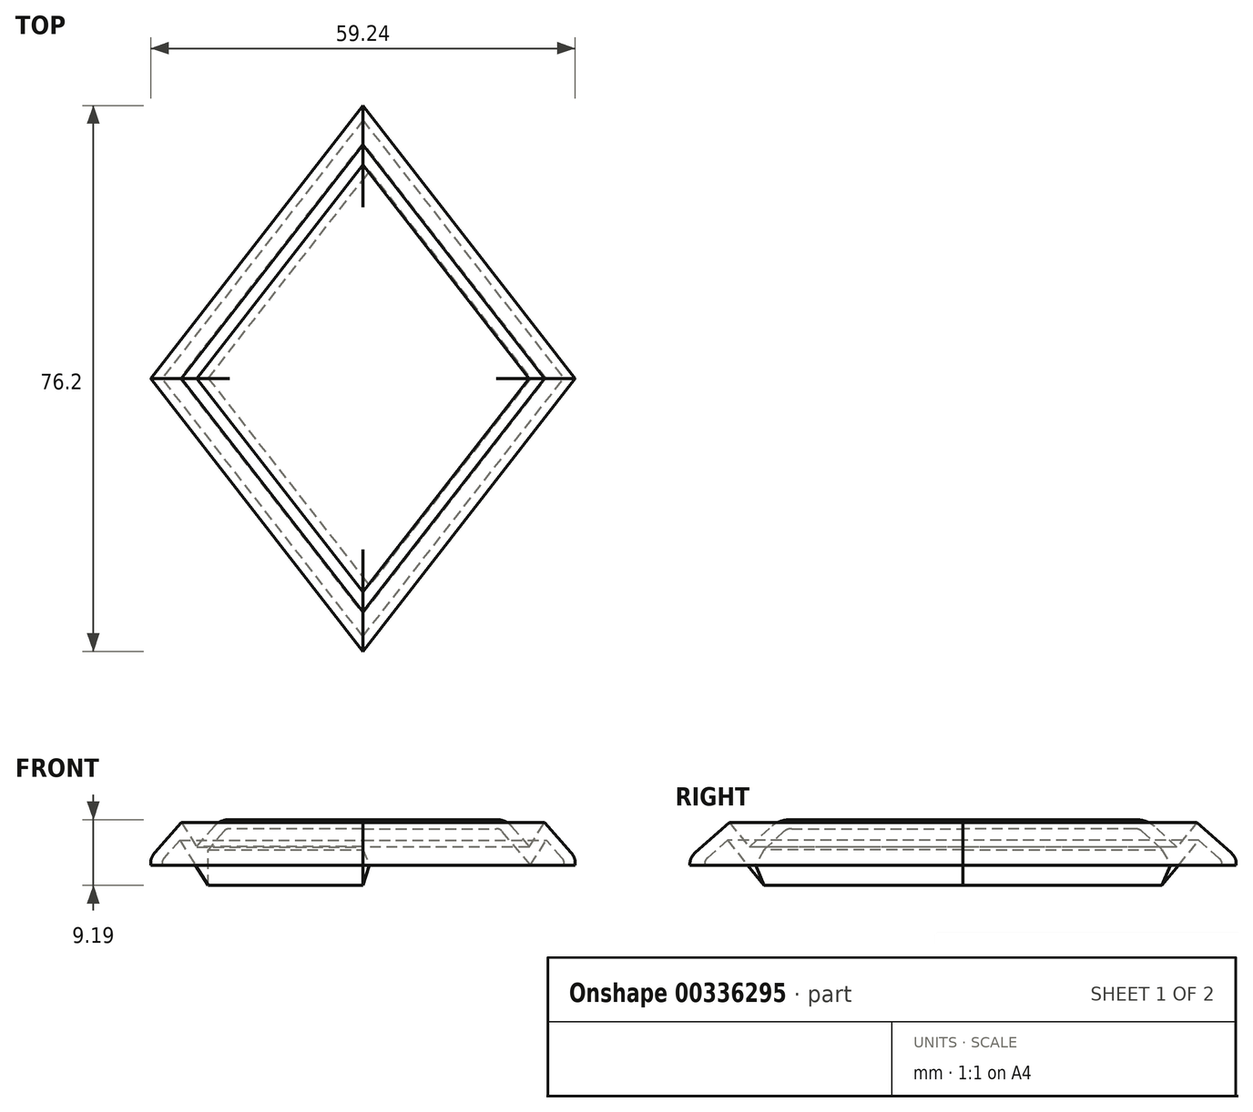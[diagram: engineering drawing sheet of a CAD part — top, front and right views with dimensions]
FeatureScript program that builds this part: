
annotation { "Feature Type Name" : "Feature", "Feature Type Description" : "" }
export const myFeature = defineFeature(function(context is Context, id is Id, definition is map)
    precondition{}
    {
        {
            var Q0;
            Q0=qCreatedBy(makeId("Top.planeOp"),FACE);
            var sketch = newSketch(context, id + "F0", { "sketchPlane" : qUnion([Q0])});
            skLineSegment(sketch, "E0", {"start": v(0, 38.1) * mm, "end": v(-29.62, 0) * mm});
            skLineSegment(sketch, "E1.MirrorCS", {"start": v(0, 38.1) * mm, "end": v(29.62, 0) * mm});
            skLineSegment(sketch, "E2.MirrorCS", {"start": v(0, -38.1) * mm, "end": v(-29.62, 0) * mm});
            skLineSegment(sketch, "E3.MirrorCS", {"start": v(0, -38.1) * mm, "end": v(29.62, 0) * mm});
            skLineSegment(sketch, "E4.0", {"start": v(0, -29.82) * mm, "end": v(23.18, 0) * mm});
            skLineSegment(sketch, "E4.1", {"start": v(0, -29.82) * mm, "end": v(-23.18, 0) * mm});
            skLineSegment(sketch, "E4.2", {"start": v(0, 29.82) * mm, "end": v(-23.18, 0) * mm});
            skLineSegment(sketch, "E4.3", {"start": v(0, 29.82) * mm, "end": v(23.18, 0) * mm});
            skSolve(sketch);
        }
        {
            var Q0;
            Q0=makeQuery(id+"F0.imprint","IMPRINT",FACE,{"disambiguationData":[TD([[makeQuery(id+"F0.imprint","IMPRINT",EDGE,{"derivedFrom":sQuery(id+"F0.wireOp",EDGE,"E0")}),1.0]])]});
            extrude(context, id + "F1", {"entities" : qUnion([Q0]), "depth" : 7.62 * mm});
        }
        {
            var Q0;
            Q0=makeQuery(id+"F1.opExtrude","CAP_EDGE",EDGE,{"disambiguationData":[OSD([sQuery(id+"F0.wireOp",EDGE,"E0")])],"isStart":false});
            var Q1;
            Q1=makeQuery(id+"F1.opExtrude","CAP_EDGE",EDGE,{"disambiguationData":[OSD([sQuery(id+"F0.wireOp",EDGE,"E2.MirrorCS")])],"isStart":false});
            var Q2;
            Q2=makeQuery(id+"F1.opExtrude","CAP_EDGE",EDGE,{"disambiguationData":[OSD([sQuery(id+"F0.wireOp",EDGE,"E3.MirrorCS")])],"isStart":false});
            var Q3;
            Q3=makeQuery(id+"F1.opExtrude","CAP_EDGE",EDGE,{"disambiguationData":[OSD([sQuery(id+"F0.wireOp",EDGE,"E1.MirrorCS")])],"isStart":false});
            chamfer(context, id + "F2", {"entities" : qUnion([Q0, Q1, Q2, Q3]), "chamferType" : ChamferType.OFFSET_ANGLE, "width" : 4.57 * mm, "oppositeDirection" : false, "angle" : 55 * degree, "tangentPropagation" : true});
        }
        {
            var Q0;
            Q0=makeQuery(id+"F1.opExtrude","CAP_EDGE",EDGE,{"disambiguationData":[OSD([sQuery(id+"F0.wireOp",EDGE,"E4.3")])],"isStart":false});
            var Q1;
            Q1=makeQuery(id+"F1.opExtrude","CAP_EDGE",EDGE,{"disambiguationData":[OSD([sQuery(id+"F0.wireOp",EDGE,"E4.2")])],"isStart":false});
            var Q2;
            Q2=makeQuery(id+"F1.opExtrude","CAP_EDGE",EDGE,{"disambiguationData":[OSD([sQuery(id+"F0.wireOp",EDGE,"E4.1")])],"isStart":false});
            var Q3;
            Q3=makeQuery(id+"F1.opExtrude","CAP_EDGE",EDGE,{"disambiguationData":[OSD([sQuery(id+"F0.wireOp",EDGE,"E4.0")])],"isStart":false});
            chamfer(context, id + "F3", {"entities" : qUnion([Q0, Q1, Q2, Q3]), "chamferType" : ChamferType.TWO_OFFSETS, "width1" : 2.54 * mm, "oppositeDirection" : false, "width2" : 5.08 * mm, "tangentPropagation" : true});
        }
        {
            var Q0;
            Q0=makeQuery(id+"F0.imprint","IMPRINT",FACE,{"disambiguationData":[TD([[makeQuery(id+"F0.imprint","IMPRINT",EDGE,{"derivedFrom":sQuery(id+"F0.wireOp",EDGE,"E4.2")}),1.0]])]});
            extrude(context, id + "F4", {"entities" : qUnion([Q0]), "depth" : 6.35 * mm});
        }
        {
            var Q0;
            Q0=makeQuery(id+"F4.opExtrude","CAP_FACE",FACE,{"disambiguationData":[OSD([sQuery(id+"F0.wireOp",EDGE,"E4.2"),sQuery(id+"F0.wireOp",EDGE,"E4.3"),sQuery(id+"F0.wireOp",EDGE,"E4.0"),sQuery(id+"F0.wireOp",EDGE,"E4.1")])],"isStart":false});
            chamfer(context, id + "F5", {"entities" : qUnion([Q0]), "chamferType" : ChamferType.TWO_OFFSETS, "width1" : 2.54 * mm, "oppositeDirection" : false, "width2" : 3.8 * mm, "tangentPropagation" : true});
        }
        {
            var Q0;
            Q0=makeQuery(id+"F4.opExtrude","CAP_FACE",FACE,{"disambiguationData":[OSD([sQuery(id+"F0.wireOp",EDGE,"E4.2"),sQuery(id+"F0.wireOp",EDGE,"E4.3"),sQuery(id+"F0.wireOp",EDGE,"E4.0"),sQuery(id+"F0.wireOp",EDGE,"E4.1")])],"isStart":false});
            fillet(context, id + "F6", {"entities" : qUnion([Q0]), "radius" : 2.03 * mm, "tangentPropagation" : true, "allowEdgeOverflow" : false});
        }
        {
            var Q0;
            {var subQ0=sQuery(id+"F0.wireOp",EDGE,"E2.MirrorCS");Q0=makeQuery(id+"F2.opChamfer","BLEND_EDGE",EDGE,{"blendedFrom":[makeQuery(id+"F1.opExtrude","CAP_EDGE",EDGE,{"disambiguationData":[OSD([subQ0])],"isStart":false}),makeQuery(id+"F1.opExtrude","SWEPT_FACE",FACE,{"disambiguationData":[OSD([subQ0])]})],"blendedInto":[makeQuery(id+"F1.opExtrude","SWEPT_FACE",FACE,{"disambiguationData":[OSD([subQ0])]})]});}
            var Q1;
            {var subQ0=sQuery(id+"F0.wireOp",EDGE,"E0");Q1=makeQuery(id+"F2.opChamfer","BLEND_EDGE",EDGE,{"blendedFrom":[makeQuery(id+"F1.opExtrude","CAP_EDGE",EDGE,{"disambiguationData":[OSD([subQ0])],"isStart":false}),makeQuery(id+"F1.opExtrude","SWEPT_FACE",FACE,{"disambiguationData":[OSD([subQ0])]})],"blendedInto":[makeQuery(id+"F1.opExtrude","SWEPT_FACE",FACE,{"disambiguationData":[OSD([subQ0])]})]});}
            var Q2;
            {var subQ0=sQuery(id+"F0.wireOp",EDGE,"E1.MirrorCS");Q2=makeQuery(id+"F2.opChamfer","BLEND_EDGE",EDGE,{"blendedFrom":[makeQuery(id+"F1.opExtrude","CAP_EDGE",EDGE,{"disambiguationData":[OSD([subQ0])],"isStart":false}),makeQuery(id+"F1.opExtrude","SWEPT_FACE",FACE,{"disambiguationData":[OSD([subQ0])]})],"blendedInto":[makeQuery(id+"F1.opExtrude","SWEPT_FACE",FACE,{"disambiguationData":[OSD([subQ0])]})]});}
            var Q3;
            {var subQ0=sQuery(id+"F0.wireOp",EDGE,"E3.MirrorCS");Q3=makeQuery(id+"F2.opChamfer","BLEND_EDGE",EDGE,{"blendedFrom":[makeQuery(id+"F1.opExtrude","CAP_EDGE",EDGE,{"disambiguationData":[OSD([subQ0])],"isStart":false}),makeQuery(id+"F1.opExtrude","SWEPT_FACE",FACE,{"disambiguationData":[OSD([subQ0])]})],"blendedInto":[makeQuery(id+"F1.opExtrude","SWEPT_FACE",FACE,{"disambiguationData":[OSD([subQ0])]})]});}
            fillet(context, id + "F7", {"entities" : qUnion([Q0, Q1, Q2, Q3]), "radius" : 2.54 * mm, "tangentPropagation" : true, "allowEdgeOverflow" : false});
        }
        {
            var Q0;
            Q0=makeQuery(id+"F4.opExtrude","SWEPT_BODY",BODY,{"disambiguationData":[OSD([sQuery(id+"F0.wireOp",EDGE,"E4.2"),sQuery(id+"F0.wireOp",EDGE,"E4.3"),sQuery(id+"F0.wireOp",EDGE,"E4.0"),sQuery(id+"F0.wireOp",EDGE,"E4.1")])]});
            var Q1;
            Q1=makeQuery(id+"F1.opExtrude","SWEPT_BODY",BODY,{"disambiguationData":[OSD([sQuery(id+"F0.wireOp",EDGE,"E0"),sQuery(id+"F0.wireOp",EDGE,"E1.MirrorCS"),sQuery(id+"F0.wireOp",EDGE,"E2.MirrorCS"),sQuery(id+"F0.wireOp",EDGE,"E3.MirrorCS"),sQuery(id+"F0.wireOp",EDGE,"E4.2"),sQuery(id+"F0.wireOp",EDGE,"E4.3"),sQuery(id+"F0.wireOp",EDGE,"E4.0"),sQuery(id+"F0.wireOp",EDGE,"E4.1")])]});
            booleanBodies(context, id + "F8", {"operationType" : BooleanOperationType.UNION, "tools" : qUnion([Q0, Q1])});
        }
        {
            var Q0;
            {var subQ0=sQuery(id+"F0.wireOp",EDGE,"E4.1");var subQ1=sQuery(id+"F0.wireOp",EDGE,"E4.0");var subQ2=sQuery(id+"F0.wireOp",EDGE,"E4.3");var subQ3=sQuery(id+"F0.wireOp",EDGE,"E4.2");Q0=makeQuery(id+"F8.opBoolean","MERGE",FACE,{"derivedFrom":[makeQuery(id+"F1.opExtrude","CAP_FACE",FACE,{"disambiguationData":[OSD([sQuery(id+"F0.wireOp",EDGE,"E0"),sQuery(id+"F0.wireOp",EDGE,"E1.MirrorCS"),sQuery(id+"F0.wireOp",EDGE,"E2.MirrorCS"),sQuery(id+"F0.wireOp",EDGE,"E3.MirrorCS"),subQ3,subQ2,subQ1,subQ0])],"isStart":true}),makeQuery(id+"F4.opExtrude","CAP_FACE",FACE,{"disambiguationData":[OSD([subQ3,subQ2,subQ1,subQ0])],"isStart":true})]});}
            shell(context, id + "F9", {"entities" : qUnion([Q0]), "thickness" : 1.27 * mm});
        }
    });
